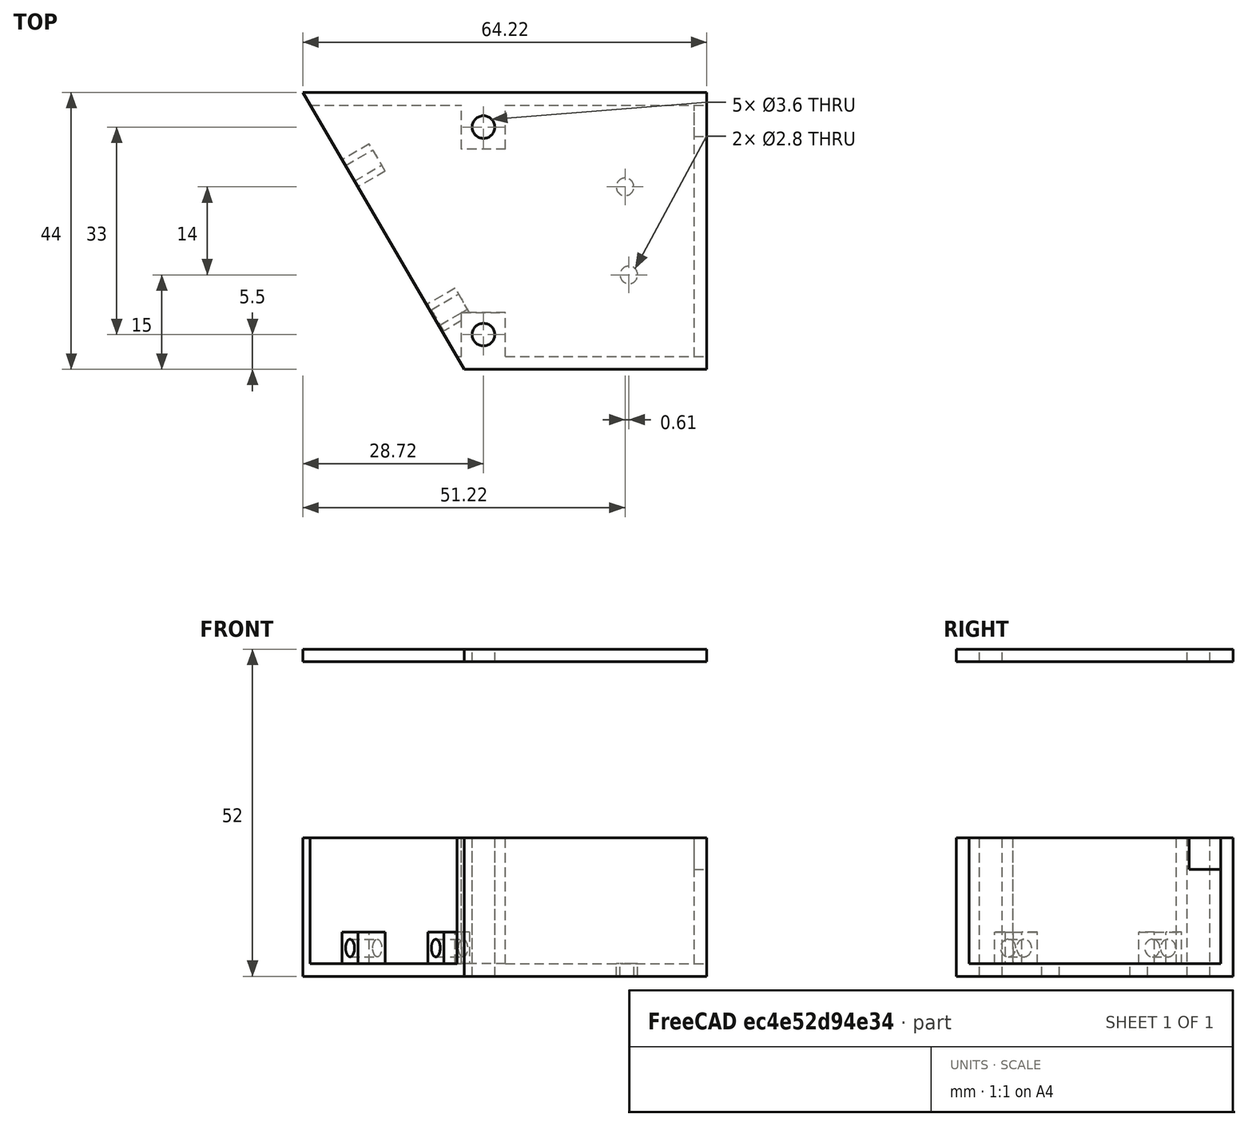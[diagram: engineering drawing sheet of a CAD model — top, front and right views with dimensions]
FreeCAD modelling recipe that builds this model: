
FCSTD DOCUMENT  (FreeCAD 0.15R4671 (Git))
Label: spektrometer 5cm entgültig total fertig verbunden
License: All rights reserved
LicenseURL: http://en.wikipedia.org/wiki/All_rights_reserved
objects: Part::Cut×14, Part::Box×8, Part::MultiFuse×6, Part::Cylinder×4
note: 32 computed .brp shape members not serialized (recipe doc carries the construction recipe); baked Part::Feature solids carry a one-line shape summary decoded from their .brp

FEATURE [Part::Box] Box  label="Würfel"
  Height = 2
  Length = 65
  Width = 44
FEATURE [Part::Box] Box001  label="Würfel001"
  Height = 25
  Length = 25
  Placement = pos=(8,-18,0) rot=(0,0,1;0.527962rad)
  Width = 60
FEATURE [Part::Box] Box002  label="Würfel002"
  Height = 20
  Length = 65
  Placement = pos=(0,42,2) rot=(0,0,1;0rad)
  Width = 2
FEATURE [Part::Box] Box003  label="Würfel003"
  Height = 20
  Length = 65
  Placement = pos=(0,0,2) rot=(0,1,0;1.5708rad)
  Width = 2
FEATURE [Part::Cut] Cut
  Base = -> Box
  Tool = -> Box001
FEATURE [Part::Cut] Cut001
  Base = -> Box003
  Tool = -> Box001
FEATURE [Part::Cut] Cut002
  Base = -> Box002
  Tool = -> Box001
FEATURE [Part::Cut] Cut003
  Base = -> Box
  Placement = pos=(0,0,50) rot=(0,0,1;0rad)
  Tool = -> Box001
FEATURE [Part::Box] Box004  label="Würfel004"
  Height = 20
  Length = 2
  Placement = pos=(63,2,2) rot=(0,0,1;0rad)
  Width = 40
FEATURE [Part::Box] Box005  label="Würfel005"
  Height = 5
  Length = 2
  Placement = pos=(63,37,17) rot=(0,0,1;0rad)
  Width = 5
FEATURE [Part::Cut] Cut004
  Base = -> Box004
  Tool = -> Box005
FEATURE [Part::Cut] Cut005
  Base = -> Box
  Placement = pos=(27.49,8.59,2) rot=(0,0,1;2.09876rad)
FEATURE [Part::Cut] Cut006
  Base = -> Box
  Placement = pos=(13.8638,31.5038,2) rot=(0,0,1;2.09876rad)
FEATURE [Part::Box] Box006  label="Würfel006"
  Height = 22
  Length = 7
  Placement = pos=(26,35,0) rot=(0,0,1;0rad)
  Width = 7
FEATURE [Part::Box] Box007  label="Würfel007"
  Height = 22
  Length = 7
  Placement = pos=(26,2,0) rot=(0,0,1;0rad)
  Width = 7
FEATURE [Part::Cylinder] Cylinder  label="Zylinder"
  Angle = 360
  Height = 100
  Placement = pos=(29.5,38.5,-6) rot=(0,0,1;0rad)
  Radius = 1.8
FEATURE [Part::Cylinder] Cylinder001  label="Zylinder001"
  Angle = 360
  Height = 100
  Placement = pos=(29.5,5.5,-6) rot=(0,0,1;0rad)
  Radius = 1.8
FEATURE [Part::Cut] Cut007
  Base = -> Cut003
  Tool = -> Cylinder
FEATURE [Part::Cut] Cut008
  Base = -> Cut007
  Tool = -> Cylinder001
FEATURE [Part::Cut] Cut009
  Base = -> Box007
  Tool = -> Cylinder001
FEATURE [Part::Cut] Cut010
  Base = -> Cut
  Tool = -> Cylinder001
FEATURE [Part::MultiFuse] Fusion
  Shapes = -> [Cut010,Box006]
FEATURE [Part::Cut] Cut011
  Base = -> Fusion
  Tool = -> Cylinder
FEATURE [Part::Cylinder] Cylinder002  label="Zylinder002"
  Angle = 360
  Height = 10
  Placement = pos=(52.61,15,0) rot=(0,0,1;0rad)
  Radius = 1.4
FEATURE [Part::Cylinder] Cylinder003  label="Zylinder003"
  Angle = 360
  Height = 10
  Placement = pos=(52,29,0) rot=(0,0,1;0rad)
  Radius = 1.4
FEATURE [Part::Cut] Cut012
  Base = -> Cut011
  Tool = -> Cylinder003
FEATURE [Part::Cut] Cut013
  Base = -> Cut012
  Tool = -> Cylinder002
FEATURE [Part::MultiFuse] Fusion001
  Shapes = -> [Cut013,Cut006]
FEATURE [Part::MultiFuse] Fusion002
  Shapes = -> [Fusion001,Cut002]
FEATURE [Part::MultiFuse] Fusion003
  Shapes = -> [Fusion002,Cut005]
FEATURE [Part::MultiFuse] Fusion004
  Shapes = -> [Fusion003,Cut001]
FEATURE [Part::MultiFuse] Fusion005
  Shapes = -> [Fusion004,Cut009]
